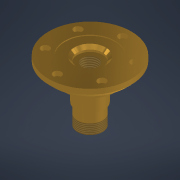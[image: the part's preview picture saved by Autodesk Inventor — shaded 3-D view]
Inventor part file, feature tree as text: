
AUTODESK INVENTOR PART (.ipt)
format: ipt  version: 2022 (Build 260153000, 153)  size: 208,384 bytes
history: native  units: mm
features: chamfer x4, sketch x3, other x3, thread x2, revolve x1, hole x1, extrude x1, reference x1, projected_geometry x1
ambient origin geometry x8: Origin, YZ Plane, XZ Plane, XY Plane, X Axis, Y Axis, Z Axis, Center Point
bodies: Solid1 (feature_tree)
feature tree (17):
  revolve  "Revolution1"  [1 undecoded]
  thread  "Thread1"  [1 undecoded]
  chamfer  "Chamfer1"  Distance=44.0mm
  chamfer  "Chamfer2"  Distance=25.0mm
  hole  "Hole1"  [1 undecoded]
  chamfer  "Chamfer4"  Distance=1.0mm
  extrude  "Extrusion1"  Depth=6.0mm
  chamfer  "Chamfer5"  Distance=5.0mm Angle=45.0deg
  thread  "Thread2"  [1 undecoded]
  sketch  "Sketch1"  dims[d3=28.0mm d4=50.0mm d7=360.0deg d8=44.0mm d9=0.0mm]
  sketch  "Sketch2"  dims[d10=16.0mm]
  reference  "Reference1"
  sketch  "Sketch3"  dims[d11=82.0mm d13=25.0mm d14=50.0mm d15=1.0mm d16=6.0mm d17=5.0mm d18=2.0mm d19=45.0deg d21=10.0mm d23=50.0mm d24=5.0mm d25=2.0mm d26=45.0deg d30=65.0mm d31=60.0mm d33=360.0deg d35=4.5mm d36=6.0mm d37=8.0mm d38=4.6mm d39=14.3117mm d40=12.0mm d41=20.594885mm d42=3.0mm d43=2.0mm d44=30.0deg d45=25.0mm d46=20.0mm d47=0.0mm d48=20.0mm d49=2.0mm d50=2.0mm d51=45.0deg d52=10.0mm d53=0.0mm d54=10.0mm d55=0.872665mm]
  projected_geometry  "Projected Loop1"
  other  "SistemaDeElevación.iam"
  other  "Bearing:2"
  other  "ISO 104 (Single Direction) 1 11 - 30 x 47 x 11:1"
note: 4 required parameter values undecoded (feature->parameter linkage not recoverable at this tier; creation-order binding heuristic only, values carry confidence <= 0.55)